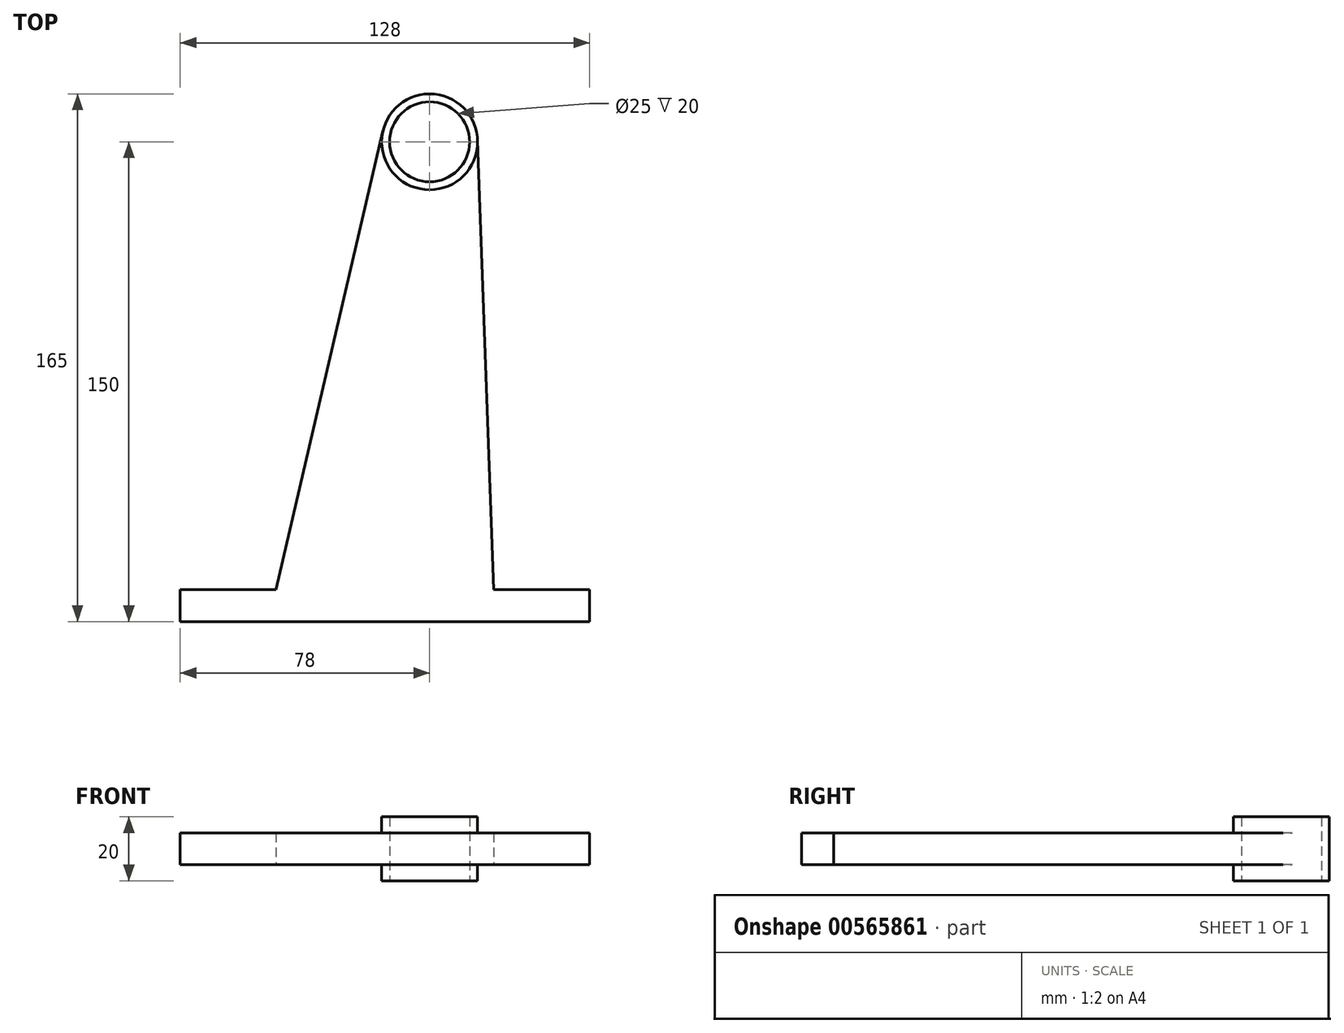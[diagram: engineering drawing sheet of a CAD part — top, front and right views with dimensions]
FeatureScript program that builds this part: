
annotation { "Feature Type Name" : "Feature", "Feature Type Description" : "" }
export const myFeature = defineFeature(function(context is Context, id is Id, definition is map)
    precondition{}
    {
        {
            var Q0;
            Q0=qCreatedBy(makeId("Top.planeOp"),FACE);
            var sketch = newSketch(context, id + "F0", { "sketchPlane" : qUnion([Q0])});
            skCircle(sketch, "E0", {"center": v(0, 0) * mm, "radius": 15 * mm});
            skLineSegment(sketch, "E1", {"start": v(-78, -150) * mm, "end": v(50, -150) * mm});
            skLineSegment(sketch, "E2", {"start": v(50, -150) * mm, "end": v(50, -140) * mm});
            skLineSegment(sketch, "E3", {"start": v(50, -140) * mm, "end": v(20, -140) * mm});
            skLineSegment(sketch, "E4", {"start": v(20, -140) * mm, "end": v(15, 0.53) * mm});
            skLineSegment(sketch, "E5", {"start": v(-78, -140) * mm, "end": v(-48, -140) * mm});
            skLineSegment(sketch, "E6", {"start": v(-48, -140) * mm, "end": v(-14.6, 3.4) * mm});
            skLineSegment(sketch, "E7", {"start": v(-78, -140) * mm, "end": v(-78, -150) * mm});
            skCircle(sketch, "E8", {"center": v(0, 0) * mm, "radius": 12.5 * mm});
            skSolve(sketch);
        }
        {
            var Q0;
            Q0=makeQuery(id+"F0.imprint","IMPRINT",FACE,{"disambiguationData":[TD([[makeQuery(id+"F0.imprint","IMPRINT",EDGE,{"derivedFrom":sQuery(id+"F0.wireOp",EDGE,"E1")}),1.0]])]});
            var Q1;
            Q1=makeQuery(id+"F0.imprint","IMPRINT",FACE,{"disambiguationData":[TD([[makeQuery(id+"F0.imprint","IMPRINT",EDGE,{"derivedFrom":sQuery(id+"F0.wireOp",EDGE,"E8")}),-1.0]])]});
            extrude(context, id + "F1", {"entities" : qUnion([Q0, Q1]), "depth" : 10 * mm, "offsetDistance" : 25 * mm});
        }
        {
            var Q0;
            Q0=makeQuery(id+"F0.imprint","IMPRINT",FACE,{"disambiguationData":[TD([[makeQuery(id+"F0.imprint","IMPRINT",EDGE,{"derivedFrom":sQuery(id+"F0.wireOp",EDGE,"E8")}),-1.0]])]});
            extrude(context, id + "F2", {"entities" : qUnion([Q0]), "operationType" : NewBodyOperationType.ADD, "depth" : 15 * mm, "offsetDistance" : 25 * mm, "hasSecondDirection" : true, "secondDirectionOppositeDirection" : true, "secondDirectionDepth" : 5 * mm});
        }
    });
